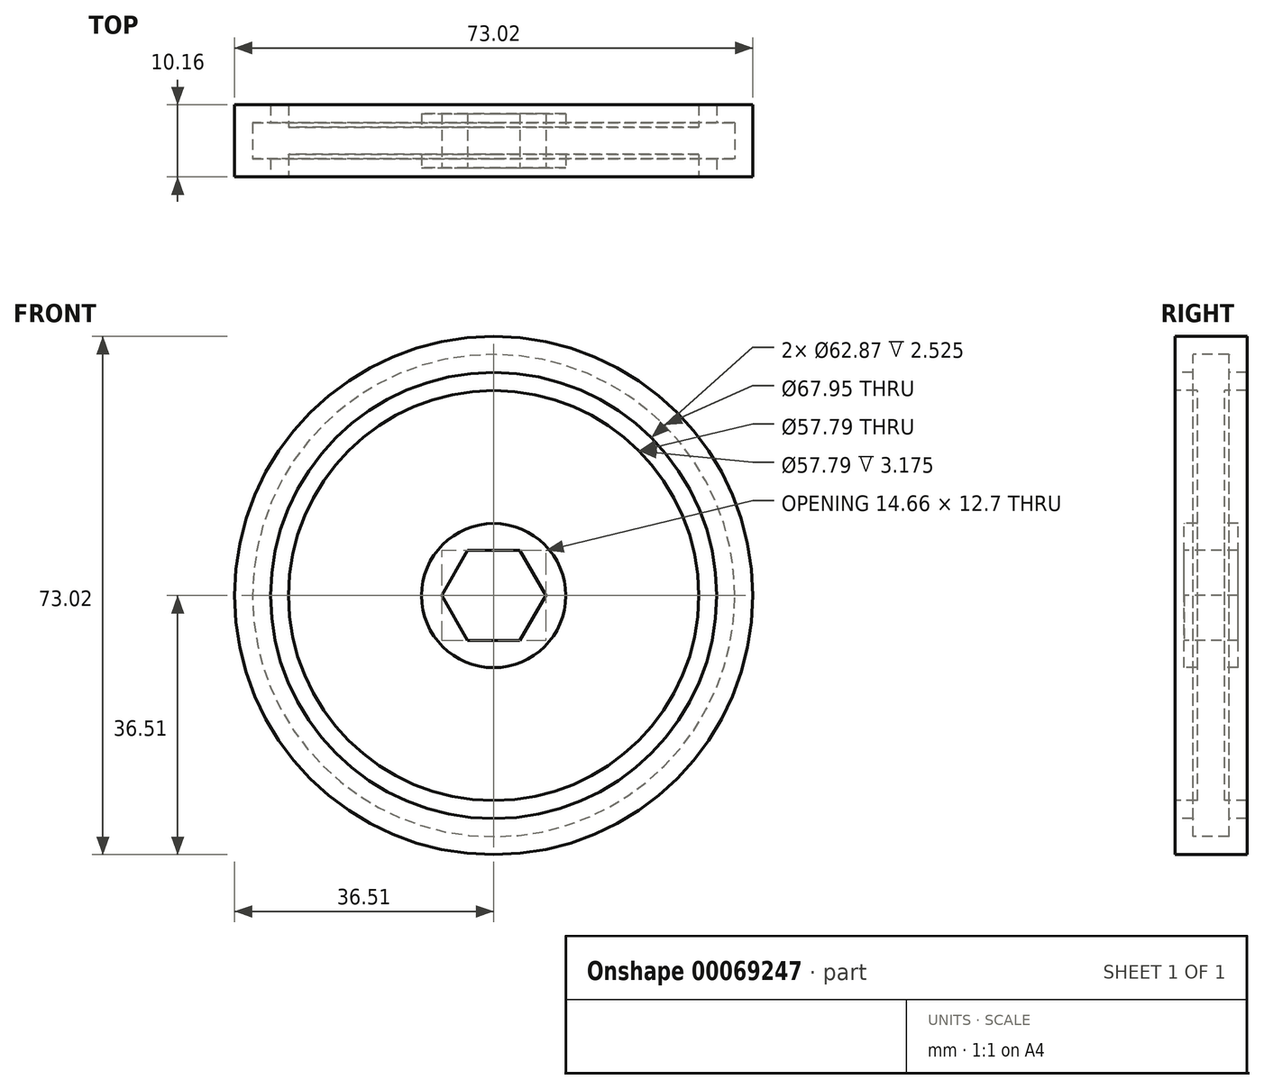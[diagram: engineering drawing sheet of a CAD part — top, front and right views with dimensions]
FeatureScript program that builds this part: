
annotation { "Feature Type Name" : "Feature", "Feature Type Description" : "" }
export const myFeature = defineFeature(function(context is Context, id is Id, definition is map)
    precondition{}
    {
        {
            var Q0;
            Q0=qCreatedBy(makeId("Top.planeOp"),FACE);
            var sketch = newSketch(context, id + "F0", { "sketchPlane" : qUnion([Q0])});
            skLineSegment(sketch, "E0.bottom", {"start": v(0, 0) * mm, "end": v(10.16, 0) * mm});
            skLineSegment(sketch, "E0.top", {"start": v(0, 3.8) * mm, "end": v(10.16, 3.8) * mm});
            skLineSegment(sketch, "E0.left", {"start": v(0, 0) * mm, "end": v(0, 3.8) * mm});
            skLineSegment(sketch, "E0.right", {"start": v(10.16, 0) * mm, "end": v(10.16, 3.8) * mm});
            skLineSegment(sketch, "E1.bottom", {"start": v(10.16, 0) * mm, "end": v(28.9, 0) * mm});
            skLineSegment(sketch, "E1.top", {"start": v(10.16, 1.9) * mm, "end": v(28.9, 1.9) * mm});
            skLineSegment(sketch, "E1.left", {"start": v(10.16, 0) * mm, "end": v(10.16, 1.9) * mm});
            skLineSegment(sketch, "E1.right", {"start": v(28.9, 0) * mm, "end": v(28.9, 1.9) * mm});
            skLineSegment(sketch, "E2.bottom", {"start": v(28.9, 0) * mm, "end": v(31.43, 0) * mm});
            skLineSegment(sketch, "E2.top", {"start": v(28.9, 5.08) * mm, "end": v(31.43, 5.08) * mm});
            skLineSegment(sketch, "E2.left", {"start": v(28.9, 0) * mm, "end": v(28.9, 5.08) * mm});
            skLineSegment(sketch, "E2.right", {"start": v(31.43, 0) * mm, "end": v(31.43, 5.08) * mm});
            skLineSegment(sketch, "E3.bottom", {"start": v(31.43, 2.54) * mm, "end": v(33.97, 2.54) * mm});
            skLineSegment(sketch, "E3.top", {"start": v(31.43, 0) * mm, "end": v(33.97, 0) * mm});
            skLineSegment(sketch, "E3.left", {"start": v(31.43, 2.54) * mm, "end": v(31.43, 0) * mm});
            skLineSegment(sketch, "E3.right", {"start": v(33.97, 2.54) * mm, "end": v(33.97, 0) * mm});
            skLineSegment(sketch, "E4.MirrorCS", {"start": v(28.9, 0) * mm, "end": v(28.9, -1.9) * mm});
            skLineSegment(sketch, "E5.MirrorCS", {"start": v(31.43, -2.54) * mm, "end": v(31.43, 0) * mm});
            skLineSegment(sketch, "E6.MirrorCS", {"start": v(31.43, -2.54) * mm, "end": v(33.97, -2.54) * mm});
            skLineSegment(sketch, "E7.MirrorCS", {"start": v(31.43, 0) * mm, "end": v(31.43, -5.08) * mm});
            skLineSegment(sketch, "E8.MirrorCS", {"start": v(28.9, 0) * mm, "end": v(28.9, -5.08) * mm});
            skLineSegment(sketch, "E9.MirrorCS", {"start": v(33.97, -2.54) * mm, "end": v(33.97, 0) * mm});
            skLineSegment(sketch, "E10.MirrorCS", {"start": v(0, -3.8) * mm, "end": v(10.16, -3.8) * mm});
            skLineSegment(sketch, "E11.MirrorCS", {"start": v(0, 0) * mm, "end": v(0, -3.8) * mm});
            skLineSegment(sketch, "E12.MirrorCS", {"start": v(10.16, 0) * mm, "end": v(10.16, -1.9) * mm});
            skLineSegment(sketch, "E13.MirrorCS", {"start": v(10.16, -1.9) * mm, "end": v(28.9, -1.9) * mm});
            skLineSegment(sketch, "E14.MirrorCS", {"start": v(28.9, -5.08) * mm, "end": v(31.43, -5.08) * mm});
            skLineSegment(sketch, "E15.MirrorCS", {"start": v(10.16, 0) * mm, "end": v(10.16, -3.8) * mm});
            skSolve(sketch);
        }
        {
            var Q0;
            Q0=makeQuery(id+"F0.imprint","IMPRINT",FACE,{"disambiguationData":[TD([[makeQuery(id+"F0.imprint","IMPRINT",EDGE,{"derivedFrom":sQuery(id+"F0.wireOp",EDGE,"E0.bottom")}),1.0]])]});
            var Q1;
            {var subQ0=sQuery(id+"F0.wireOp",EDGE,"E1.top");Q1=makeQuery(id+"F0.imprint","IMPRINT",FACE,{"disambiguationData":[TD([[makeQuery(id+"F0.imprint","IMPRINT",EDGE,{"derivedFrom":subQ0}),-1.0]])]});}
            var Q2;
            {var subQ1=sQuery(id+"F0.wireOp",EDGE,"E0.bottom");Q2=makeQuery(id+"F0.imprint","IMPRINT",FACE,{"disambiguationData":[TD([[makeQuery(id+"F0.imprint","IMPRINT",EDGE,{"derivedFrom":subQ1}),-1.0]])]});}
            var Q3;
            {var subQ2=sQuery(id+"F0.wireOp",EDGE,"E13.MirrorCS");Q3=makeQuery(id+"F0.imprint","IMPRINT",FACE,{"disambiguationData":[TD([[makeQuery(id+"F0.imprint","IMPRINT",EDGE,{"derivedFrom":subQ2}),1.0]])]});}
            var Q4;
            {var subQ0=sQuery(id+"F0.wireOp",EDGE,"E6.MirrorCS");Q4=makeQuery(id+"F0.imprint","IMPRINT",FACE,{"disambiguationData":[TD([[makeQuery(id+"F0.imprint","IMPRINT",EDGE,{"derivedFrom":subQ0}),1.0]])]});}
            var Q5;
            Q5=makeQuery(id+"F0.imprint","IMPRINT",FACE,{"disambiguationData":[TD([[makeQuery(id+"F0.imprint","IMPRINT",EDGE,{"derivedFrom":sQuery(id+"F0.wireOp",EDGE,"E3.bottom")}),-1.0]])]});
            var Q6;
            {var subQ2=sQuery(id+"F0.wireOp",EDGE,"E2.top");Q6=makeQuery(id+"F0.imprint","IMPRINT",FACE,{"disambiguationData":[TD([[makeQuery(id+"F0.imprint","IMPRINT",EDGE,{"derivedFrom":subQ2}),-1.0]])]});}
            var Q7;
            {var subQ1=sQuery(id+"F0.wireOp",EDGE,"E2.bottom");Q7=makeQuery(id+"F0.imprint","IMPRINT",FACE,{"disambiguationData":[TD([[makeQuery(id+"F0.imprint","IMPRINT",EDGE,{"derivedFrom":subQ1}),-1.0]])]});}
            var Q8;
            Q8=sQuery(id+"F0.wireOp",EDGE,"E0.left");
            revolve(context, id + "F1", {"entities" : qUnion([Q0, Q1, Q2, Q3, Q4, Q5, Q6, Q7]), "axis" : qUnion([Q8]), "revolveType" : RevolveType.FULL});
        }
        {
            var Q0;
            Q0=makeQuery(id+"F1.opRevolve","SWEPT_FACE",FACE,{"disambiguationData":[OSD([sQuery(id+"F0.wireOp",EDGE,"E10.MirrorCS")])]});
            var sketch = newSketch(context, id + "F2", { "sketchPlane" : qUnion([Q0])});
            skPoint(sketch, "E16.0", {"position": v(0, 0) * mm});
            skCircle(sketch, "E17.cCircle", {"center": v(0, 0) * mm, "radius": 6.35 * mm, "construction": true});
            skLineSegment(sketch, "E17.0", {"start": v(-3.67, 6.35) * mm, "end": v(3.67, 6.35) * mm});
            skLineSegment(sketch, "E17.1", {"start": v(3.67, 6.35) * mm, "end": v(7.33, 0) * mm});
            skLineSegment(sketch, "E17.2", {"start": v(7.33, 0) * mm, "end": v(3.67, -6.35) * mm});
            skLineSegment(sketch, "E17.3", {"start": v(3.67, -6.35) * mm, "end": v(-3.67, -6.35) * mm});
            skLineSegment(sketch, "E17.4", {"start": v(-3.67, -6.35) * mm, "end": v(-7.33, 0) * mm});
            skLineSegment(sketch, "E17.5", {"start": v(-7.33, 0) * mm, "end": v(-3.67, 6.35) * mm});
            skPoint(sketch, "E17.0.midPoint", {"position": v(0, 6.35) * mm});
            skSolve(sketch);
        }
        {
            var Q0;
            Q0=makeQuery(id+"F2.imprint","IMPRINT",FACE,{"disambiguationData":[TD([[makeQuery(id+"F2.imprint","IMPRINT",EDGE,{"derivedFrom":sQuery(id+"F2.wireOp",EDGE,"E17.0")}),-1.0]])]});
            extrude(context, id + "F3", {"entities" : qUnion([Q0]), "operationType" : NewBodyOperationType.REMOVE, "endBound" : BoundingType.THROUGH_ALL, "oppositeDirection" : true, "depth" : 25.4 * mm});
        }
        {
            var Q0;
            Q0=qCreatedBy(makeId("Top.planeOp"),FACE);
            var sketch = newSketch(context, id + "F4", { "sketchPlane" : qUnion([Q0])});
            skLineSegment(sketch, "E18.0", {"start": v(31.43, 0) * mm, "end": v(31.43, 5.08) * mm});
            skLineSegment(sketch, "E19.0", {"start": v(31.43, 2.54) * mm, "end": v(33.97, 2.54) * mm});
            skLineSegment(sketch, "E20.0", {"start": v(33.97, 2.54) * mm, "end": v(33.97, 0) * mm});
            skLineSegment(sketch, "E21.0", {"start": v(33.97, -2.54) * mm, "end": v(33.97, 0) * mm});
            skLineSegment(sketch, "E22.0", {"start": v(31.43, -2.54) * mm, "end": v(33.97, -2.54) * mm});
            skLineSegment(sketch, "E23.0", {"start": v(31.43, 0) * mm, "end": v(31.43, -5.08) * mm});
            skLineSegment(sketch, "E24", {"start": v(31.43, 5.08) * mm, "end": v(36.51, 5.08) * mm});
            skLineSegment(sketch, "E25", {"start": v(36.51, 5.08) * mm, "end": v(36.51, -5.08) * mm});
            skLineSegment(sketch, "E26", {"start": v(36.51, -5.08) * mm, "end": v(31.43, -5.08) * mm});
            skSolve(sketch);
        }
        {
            var Q0;
            {var subQ2=sQuery(id+"F4.wireOp",EDGE,"E19.0");Q0=makeQuery(id+"F4.imprint","IMPRINT",FACE,{"disambiguationData":[TD([[makeQuery(id+"F4.imprint","IMPRINT",EDGE,{"derivedFrom":subQ2}),1.0]])]});}
            var Q1;
            Q1=sQuery(id+"F0.wireOp",EDGE,"E0.left");
            revolve(context, id + "F5", {"entities" : qUnion([Q0]), "axis" : qUnion([Q1]), "revolveType" : RevolveType.FULL});
        }
        {
            assignVariable(context, id + "F6", {"name" : "fillet_a", "anyValue" : 0.05});
        }
        {
            assignVariable(context, id + "F7", {"name" : "fillet_b", "anyValue" : 0.01});
        }
        {
            var Q0;
            Q0=makeQuery(id+"F1.opRevolve","SWEPT_EDGE",EDGE,{"disambiguationData":[OSD([sQuery(id+"F0.wireOp",EDGE,"E8.MirrorCS"),sQuery(id+"F0.wireOp",EDGE,"E13.MirrorCS")])]});
            var Q1;
            Q1=makeQuery(id+"F1.opRevolve","SWEPT_EDGE",EDGE,{"disambiguationData":[OSD([sQuery(id+"F0.wireOp",EDGE,"E13.MirrorCS"),sQuery(id+"F0.wireOp",EDGE,"E15.MirrorCS")])]});
            fillet(context, id + "F8", {"entities" : qUnion([Q0, Q1]), "radius" : (getVariable(context, 'fillet_a')) * mm, "tangentPropagation" : true, "allowEdgeOverflow" : false});
        }
        {
            var Q0;
            Q0=makeQuery(id+"F1.opRevolve","SWEPT_EDGE",EDGE,{"disambiguationData":[OSD([sQuery(id+"F0.wireOp",EDGE,"E8.MirrorCS"),sQuery(id+"F0.wireOp",EDGE,"E14.MirrorCS")])]});
            var Q1;
            Q1=makeQuery(id+"F1.opRevolve","SWEPT_EDGE",EDGE,{"disambiguationData":[OSD([sQuery(id+"F0.wireOp",EDGE,"E10.MirrorCS"),sQuery(id+"F0.wireOp",EDGE,"E15.MirrorCS")])]});
            fillet(context, id + "F9", {"entities" : qUnion([Q0, Q1]), "radius" : (getVariable(context, 'fillet_b')) * mm, "tangentPropagation" : true, "allowEdgeOverflow" : false});
        }
        {
            var Q0;
            Q0=makeQuery(id+"F1.opRevolve","SWEPT_EDGE",EDGE,{"disambiguationData":[OSD([sQuery(id+"F0.wireOp",EDGE,"E6.MirrorCS"),sQuery(id+"F0.wireOp",EDGE,"E7.MirrorCS")])]});
            var Q1;
            Q1=makeQuery(id+"F1.opRevolve","SWEPT_EDGE",EDGE,{"disambiguationData":[OSD([sQuery(id+"F0.wireOp",EDGE,"E6.MirrorCS"),sQuery(id+"F0.wireOp",EDGE,"E9.MirrorCS")])]});
            var Q2;
            Q2=makeQuery(id+"F1.opRevolve","SWEPT_EDGE",EDGE,{"disambiguationData":[OSD([sQuery(id+"F0.wireOp",EDGE,"E2.right"),sQuery(id+"F0.wireOp",EDGE,"E3.bottom"),sQuery(id+"F0.wireOp",EDGE,"E3.left")])]});
            var Q3;
            Q3=makeQuery(id+"F1.opRevolve","SWEPT_EDGE",EDGE,{"disambiguationData":[OSD([sQuery(id+"F0.wireOp",EDGE,"E3.bottom"),sQuery(id+"F0.wireOp",EDGE,"E3.right")])]});
            fillet(context, id + "F10", {"entities" : qUnion([Q0, Q1, Q2, Q3]), "radius" : (getVariable(context, 'fillet_b')) * mm, "tangentPropagation" : true, "allowEdgeOverflow" : false});
        }
        {
            var Q0;
            Q0=makeQuery(id+"F5.opRevolve","SWEPT_EDGE",EDGE,{"disambiguationData":[OSD([sQuery(id+"F4.wireOp",EDGE,"E19.0"),sQuery(id+"F4.wireOp",EDGE,"E20.0")])]});
            var Q1;
            Q1=makeQuery(id+"F5.opRevolve","SWEPT_EDGE",EDGE,{"disambiguationData":[OSD([sQuery(id+"F4.wireOp",EDGE,"E18.0"),sQuery(id+"F4.wireOp",EDGE,"E19.0")])]});
            var Q2;
            Q2=makeQuery(id+"F5.opRevolve","SWEPT_EDGE",EDGE,{"disambiguationData":[OSD([sQuery(id+"F4.wireOp",EDGE,"E22.0"),sQuery(id+"F4.wireOp",EDGE,"E23.0")])]});
            var Q3;
            Q3=makeQuery(id+"F5.opRevolve","SWEPT_EDGE",EDGE,{"disambiguationData":[OSD([sQuery(id+"F4.wireOp",EDGE,"E21.0"),sQuery(id+"F4.wireOp",EDGE,"E22.0")])]});
            fillet(context, id + "F11", {"entities" : qUnion([Q0, Q1, Q2, Q3]), "radius" : (getVariable(context, 'fillet_b')) * mm, "tangentPropagation" : true, "allowEdgeOverflow" : false});
        }
    });
